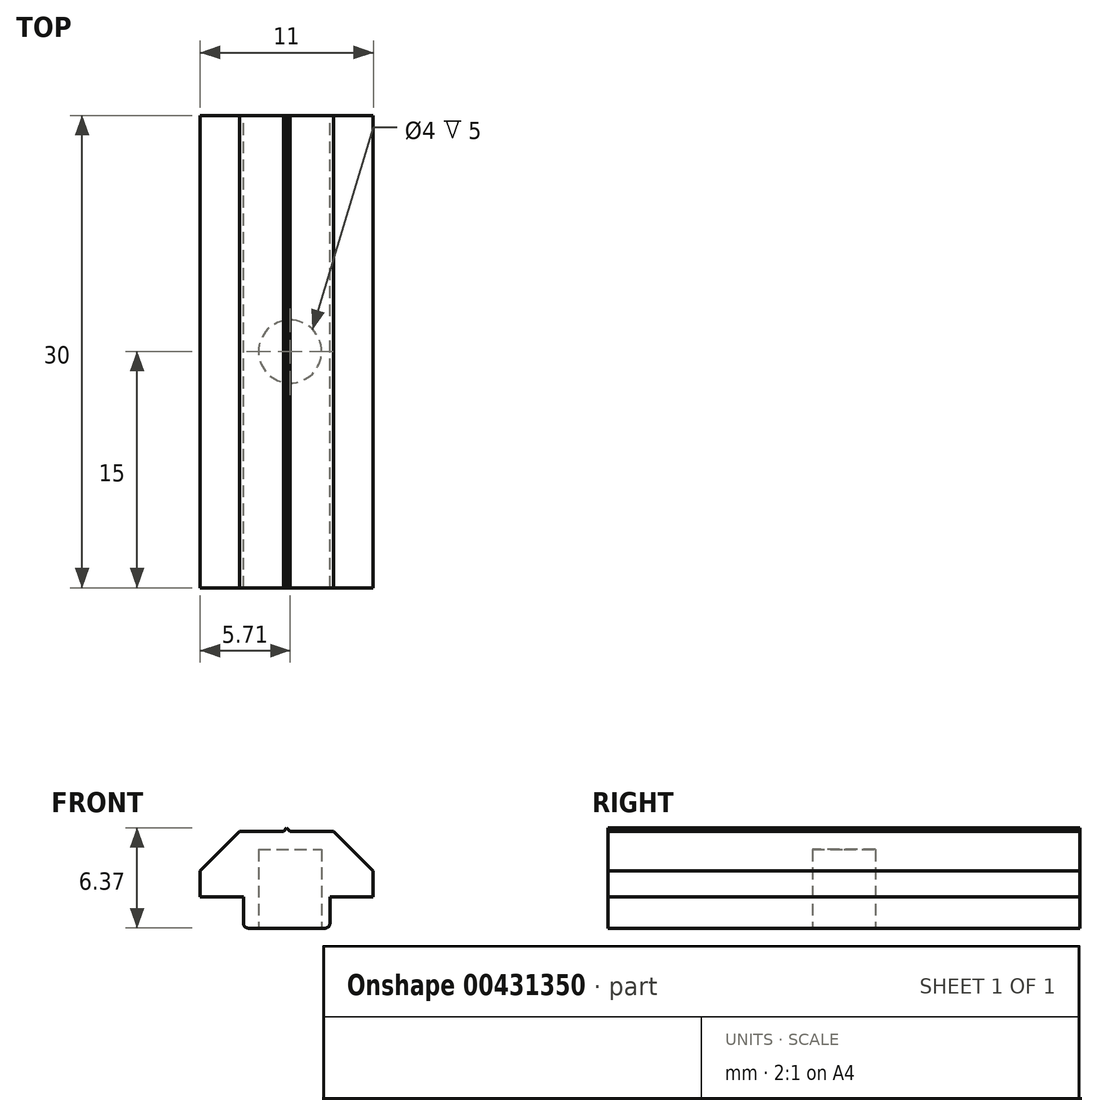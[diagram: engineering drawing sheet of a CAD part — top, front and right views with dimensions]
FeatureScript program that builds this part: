
annotation { "Feature Type Name" : "Feature", "Feature Type Description" : "" }
export const myFeature = defineFeature(function(context is Context, id is Id, definition is map)
    precondition{}
    {
        {
            var Q0;
            Q0=qCreatedBy(makeId("Front.planeOp"),FACE);
            var sketch = newSketch(context, id + "F0", { "sketchPlane" : qUnion([Q0])});
            skLineSegment(sketch, "E0", {"start": v(-53.24, 27.05) * mm, "end": v(-50.47, 27.05) * mm});
            skLineSegment(sketch, "E1", {"start": v(-50.47, 27.05) * mm, "end": v(-50.26, 27.27) * mm});
            skLineSegment(sketch, "E2", {"start": v(-50.26, 27.27) * mm, "end": v(-50.05, 27.05) * mm});
            skLineSegment(sketch, "E3", {"start": v(-50.05, 27.05) * mm, "end": v(-47.28, 27.05) * mm});
            skLineSegment(sketch, "E4", {"start": v(-47.28, 27.05) * mm, "end": v(-44.76, 24.54) * mm});
            skLineSegment(sketch, "E5", {"start": v(-44.76, 24.54) * mm, "end": v(-44.76, 22.9) * mm});
            skLineSegment(sketch, "E6.MirrorCS", {"start": v(-53.24, 27.05) * mm, "end": v(-55.76, 24.54) * mm});
            skLineSegment(sketch, "E7.MirrorCS", {"start": v(-55.76, 24.54) * mm, "end": v(-55.76, 22.9) * mm});
            skLineSegment(sketch, "E8", {"start": v(-55.76, 22.9) * mm, "end": v(-53.01, 22.9) * mm});
            skLineSegment(sketch, "E9", {"start": v(-47.51, 22.9) * mm, "end": v(-47.51, 21.22) * mm});
            skLineSegment(sketch, "E10", {"start": v(-47.84, 20.9) * mm, "end": v(-52.69, 20.9) * mm});
            skLineSegment(sketch, "E11", {"start": v(-53.01, 21.22) * mm, "end": v(-53.01, 22.9) * mm});
            skPoint(sketch, "E12.visualSharp", {"position": v(-47.51, 20.9) * mm});
            skArc(sketch, "E12.filletArc", {"start": v(-47.84, 20.9) * mm, "mid": v(-47.6, 21) * mm, "end": v(-47.51, 21.22) * mm});
            skPoint(sketch, "E13.visualSharp", {"position": v(-53.01, 20.9) * mm});
            skArc(sketch, "E13.filletArc", {"start": v(-53.01, 21.22) * mm, "mid": v(-52.92, 21) * mm, "end": v(-52.69, 20.9) * mm});
            skLineSegment(sketch, "E14.trimOffspring", {"start": v(-47.51, 22.9) * mm, "end": v(-44.76, 22.9) * mm});
            skSolve(sketch);
        }
        {
            var Q0;
            Q0 = qSketchRegion(id + "F0", true);
            extrude(context, id + "F1", {"entities" : qUnion([Q0]), "depth" : 30 * mm});
        }
        {
            var Q0;
            Q0=makeQuery(id+"F1.opExtrude","SWEPT_FACE",FACE,{"disambiguationData":[OSD([sQuery(id+"F0.wireOp",EDGE,"E10")])]});
            var sketch = newSketch(context, id + "F2", { "sketchPlane" : qUnion([Q0])});
            skCircle(sketch, "E15", {"center": v(-50.05, 15) * mm, "radius": 2 * mm});
            skSolve(sketch);
        }
        {
            var Q0;
            Q0 = qSketchRegion(id + "F2", true);
            extrude(context, id + "F3", {"entities" : qUnion([Q0]), "operationType" : NewBodyOperationType.REMOVE, "oppositeDirection" : true, "depth" : 5 * mm});
        }
    });
